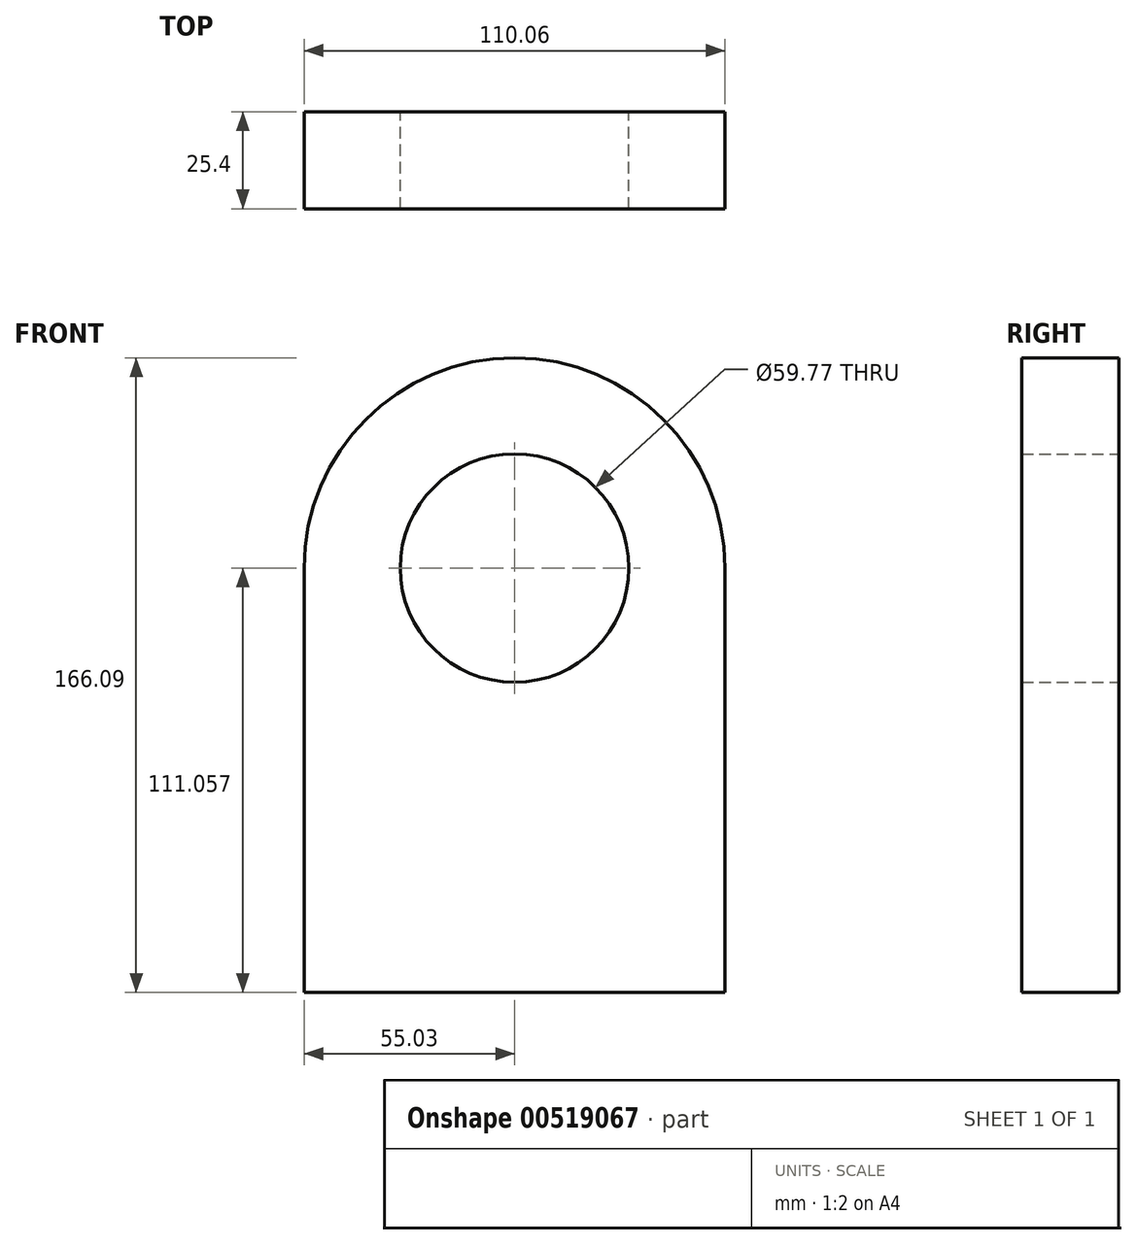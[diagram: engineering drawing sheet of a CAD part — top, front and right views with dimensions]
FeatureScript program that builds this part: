
annotation { "Feature Type Name" : "Feature", "Feature Type Description" : "" }
export const myFeature = defineFeature(function(context is Context, id is Id, definition is map)
    precondition{}
    {
        {
            var Q0;
            Q0=qCreatedBy(makeId("Front.planeOp"),FACE);
            var sketch = newSketch(context, id + "F0", { "sketchPlane" : qUnion([Q0])});
            skLineSegment(sketch, "E0.bottom", {"start": v(55.03, -55.53) * mm, "end": v(-55.03, -55.53) * mm});
            skLineSegment(sketch, "E0.top", {"start": v(55.03, 55.53) * mm, "end": v(55.03, 55.53) * mm});
            skLineSegment(sketch, "E0.left", {"start": v(55.03, -55.53) * mm, "end": v(55.03, 55.53) * mm});
            skLineSegment(sketch, "E0.right", {"start": v(-55.03, -55.53) * mm, "end": v(-55.03, 55.53) * mm});
            skPoint(sketch, "E0.middle", {"position": v(0, 0) * mm});
            skArc(sketch, "E1", {"start": v(55.03, 55.53) * mm, "mid": v(0, 110.56) * mm, "end": v(-55.03, 55.53) * mm});
            skCircle(sketch, "E2.0", {"center": v(0, 55.53) * mm, "radius": 29.88 * mm});
            skLineSegment(sketch, "E3.trimOffspring", {"start": v(-55.03, 55.53) * mm, "end": v(-55.03, 55.53) * mm});
            skSolve(sketch);
        }
        {
            var Q0;
            Q0 = qSketchRegion(id + "F0", true);
            extrude(context, id + "F1", {"entities" : qUnion([Q0]), "depth" : 25.4 * mm});
        }
    });
